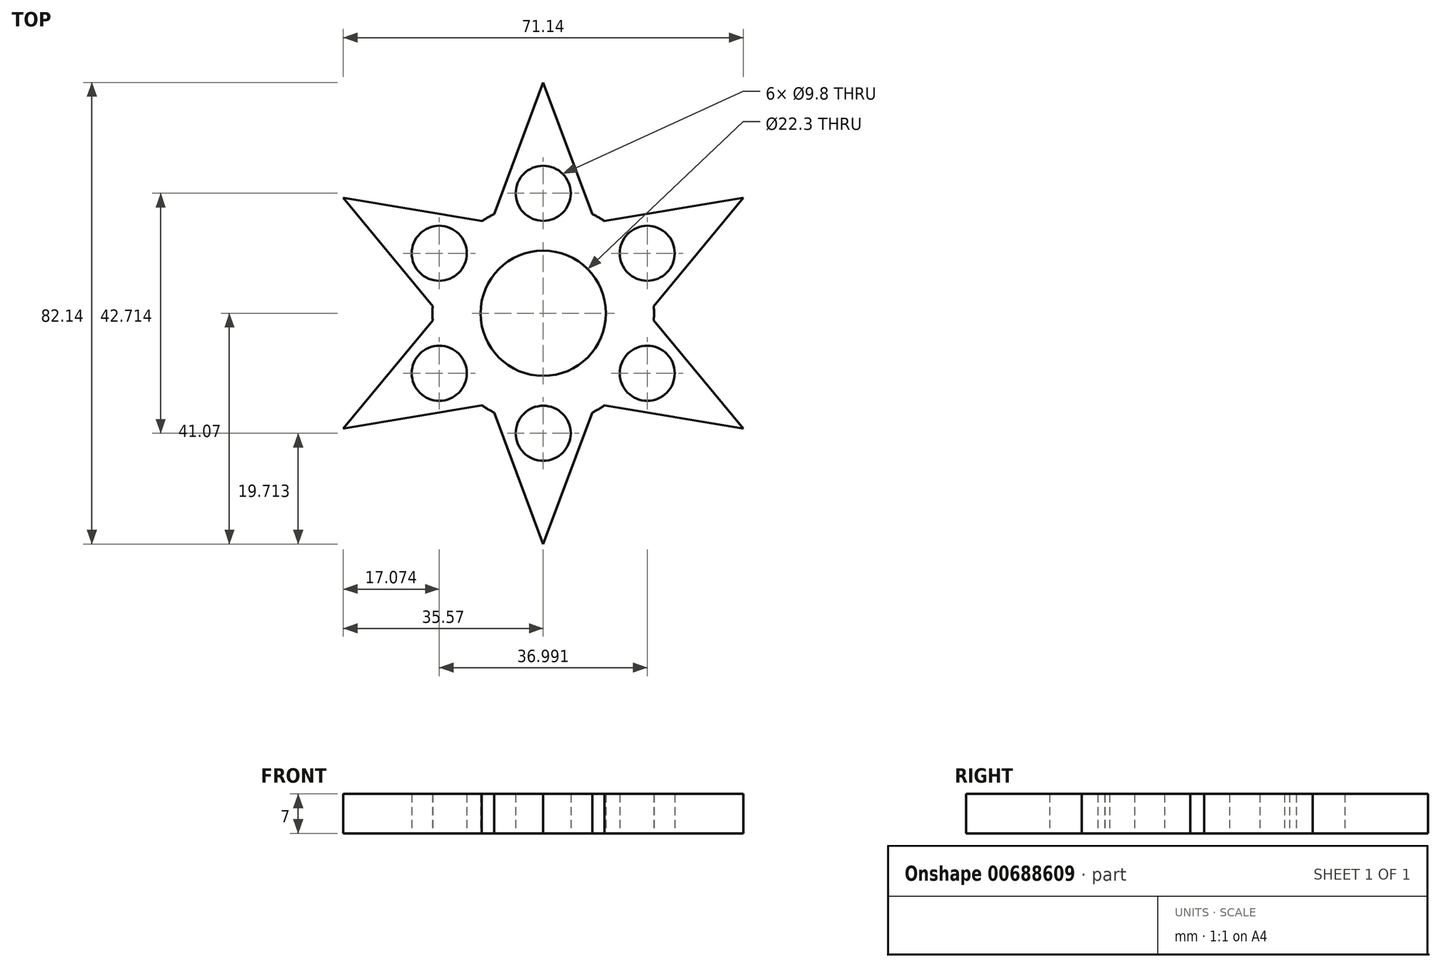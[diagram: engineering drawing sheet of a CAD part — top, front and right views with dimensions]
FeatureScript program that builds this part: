
annotation { "Feature Type Name" : "Feature", "Feature Type Description" : "" }
export const myFeature = defineFeature(function(context is Context, id is Id, definition is map)
    precondition{}
    {
        {
            var Q0;
            Q0=qCreatedBy(makeId("Top.planeOp"),FACE);
            var sketch = newSketch(context, id + "F0", { "sketchPlane" : qUnion([Q0])});
            skCircle(sketch, "E0", {"center": v(0, 0) * mm, "radius": 11.15 * mm});
            skCircle(sketch, "E1", {"center": v(0, 0) * mm, "radius": 19.7 * mm});
            skLineSegment(sketch, "E2", {"start": v(-8.75, 17.66) * mm, "end": v(0, 41.07) * mm});
            skLineSegment(sketch, "E3.MirrorCS", {"start": v(8.75, 17.66) * mm, "end": v(0, 41.07) * mm});
            skLineSegment(sketch, "E4.1.0", {"start": v(-10.92, 16.4) * mm, "end": v(-35.57, 20.54) * mm});
            skLineSegment(sketch, "E4.1.1", {"start": v(-19.66, 1.25) * mm, "end": v(-35.57, 20.54) * mm});
            skLineSegment(sketch, "E4.2.0", {"start": v(-19.66, -1.25) * mm, "end": v(-35.57, -20.54) * mm});
            skLineSegment(sketch, "E4.2.1", {"start": v(-10.92, -16.4) * mm, "end": v(-35.57, -20.54) * mm});
            skLineSegment(sketch, "E4.3.0", {"start": v(-8.75, -17.66) * mm, "end": v(0, -41.07) * mm});
            skLineSegment(sketch, "E4.3.1", {"start": v(8.75, -17.66) * mm, "end": v(0, -41.07) * mm});
            skLineSegment(sketch, "E4.4.0", {"start": v(10.92, -16.4) * mm, "end": v(35.57, -20.54) * mm});
            skLineSegment(sketch, "E4.4.1", {"start": v(19.66, -1.25) * mm, "end": v(35.57, -20.54) * mm});
            skLineSegment(sketch, "E4.5.0", {"start": v(19.66, 1.25) * mm, "end": v(35.57, 20.54) * mm});
            skLineSegment(sketch, "E4.5.1", {"start": v(10.92, 16.4) * mm, "end": v(35.57, 20.54) * mm});
            skCircle(sketch, "E5", {"center": v(0, 21.36) * mm, "radius": 4.9 * mm});
            skCircle(sketch, "E6.1.0", {"center": v(-18.5, 10.68) * mm, "radius": 4.9 * mm});
            skCircle(sketch, "E6.2.0", {"center": v(-18.5, -10.68) * mm, "radius": 4.9 * mm});
            skCircle(sketch, "E6.3.0", {"center": v(0, -21.36) * mm, "radius": 4.9 * mm});
            skCircle(sketch, "E6.4.0", {"center": v(18.5, -10.68) * mm, "radius": 4.9 * mm});
            skCircle(sketch, "E6.5.0", {"center": v(18.5, 10.68) * mm, "radius": 4.9 * mm});
            skSolve(sketch);
        }
        {
            var Q0;
            Q0=makeQuery(id+"F0.imprint","IMPRINT",FACE,{"disambiguationData":[TD([[makeQuery(id+"F0.imprint","IMPRINT",EDGE,{"derivedFrom":sQuery(id+"F0.wireOp",EDGE,"E0")}),-1.0]])]});
            var Q1;
            {var subQ0=sQuery(id+"F0.wireOp",EDGE,"E4.5.0");Q1=makeQuery(id+"F0.imprint","IMPRINT",FACE,{"disambiguationData":[TD([[makeQuery(id+"F0.imprint","IMPRINT",EDGE,{"derivedFrom":subQ0}),1.0]])]});}
            var Q2;
            {var subQ1=sQuery(id+"F0.wireOp",EDGE,"E2");Q2=makeQuery(id+"F0.imprint","IMPRINT",FACE,{"disambiguationData":[TD([[makeQuery(id+"F0.imprint","IMPRINT",EDGE,{"derivedFrom":subQ1}),-1.0]])]});}
            var Q3;
            {var subQ1=sQuery(id+"F0.wireOp",EDGE,"E4.1.0");Q3=makeQuery(id+"F0.imprint","IMPRINT",FACE,{"disambiguationData":[TD([[makeQuery(id+"F0.imprint","IMPRINT",EDGE,{"derivedFrom":subQ1}),1.0]])]});}
            var Q4;
            {var subQ0=sQuery(id+"F0.wireOp",EDGE,"E4.2.0");Q4=makeQuery(id+"F0.imprint","IMPRINT",FACE,{"disambiguationData":[TD([[makeQuery(id+"F0.imprint","IMPRINT",EDGE,{"derivedFrom":subQ0}),1.0]])]});}
            var Q5;
            {var subQ4=sQuery(id+"F0.wireOp",EDGE,"E4.4.0");Q5=makeQuery(id+"F0.imprint","IMPRINT",FACE,{"disambiguationData":[TD([[makeQuery(id+"F0.imprint","IMPRINT",EDGE,{"derivedFrom":subQ4}),1.0]])]});}
            var Q6;
            {var subQ0=sQuery(id+"F0.wireOp",EDGE,"E4.3.0");Q6=makeQuery(id+"F0.imprint","IMPRINT",FACE,{"disambiguationData":[TD([[makeQuery(id+"F0.imprint","IMPRINT",EDGE,{"derivedFrom":subQ0}),1.0]])]});}
            extrude(context, id + "F1", {"entities" : qUnion([Q0, Q1, Q2, Q3, Q4, Q5, Q6]), "depth" : 7 * mm, "offsetDistance" : 25 * mm});
        }
    });
